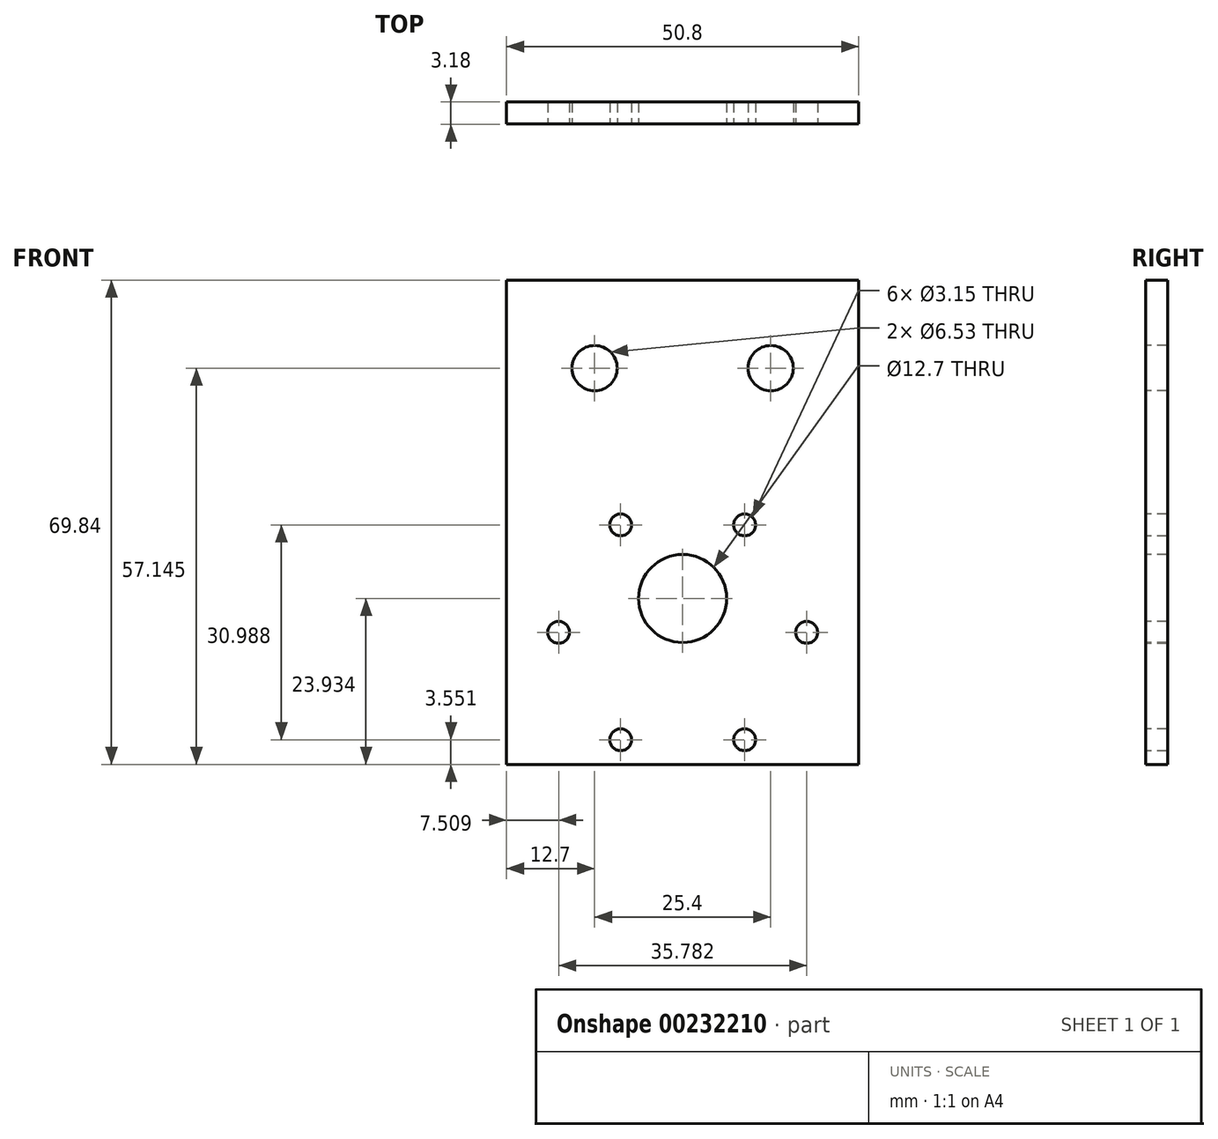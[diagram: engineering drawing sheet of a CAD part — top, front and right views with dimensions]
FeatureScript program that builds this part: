
annotation { "Feature Type Name" : "Feature", "Feature Type Description" : "" }
export const myFeature = defineFeature(function(context is Context, id is Id, definition is map)
    precondition{}
    {
        {
            var Q0;
            Q0=qCreatedBy(makeId("Front.planeOp"),FACE);
            var sketch = newSketch(context, id + "F0", { "sketchPlane" : qUnion([Q0])});
            skLineSegment(sketch, "E0.bottom", {"start": v(25.4, -34.93) * mm, "end": v(-25.4, -34.93) * mm});
            skLineSegment(sketch, "E0.top", {"start": v(25.4, 34.93) * mm, "end": v(-25.4, 34.93) * mm});
            skLineSegment(sketch, "E0.left", {"start": v(25.4, -34.93) * mm, "end": v(25.4, 34.93) * mm});
            skLineSegment(sketch, "E0.right", {"start": v(-25.4, -34.93) * mm, "end": v(-25.4, 34.93) * mm});
            skPoint(sketch, "E0.middle", {"position": v(0, 0) * mm});
            skSolve(sketch);
        }
        {
            var Q0;
            Q0=makeQuery(id+"F0.imprint","IMPRINT",FACE,{"disambiguationData":[TD([[makeQuery(id+"F0.imprint","IMPRINT",EDGE,{"derivedFrom":sQuery(id+"F0.wireOp",EDGE,"E0.bottom")}),-1.0]])]});
            extrude(context, id + "F1", {"entities" : qUnion([Q0]), "depth" : 3.17 * mm});
        }
        {
            var Q0;
            Q0=makeQuery(id+"F1.opExtrude","CAP_FACE",FACE,{"disambiguationData":[OSD([sQuery(id+"F0.wireOp",EDGE,"E0.bottom"),sQuery(id+"F0.wireOp",EDGE,"E0.top"),sQuery(id+"F0.wireOp",EDGE,"E0.left"),sQuery(id+"F0.wireOp",EDGE,"E0.right")])],"isStart":false});
            var sketch = newSketch(context, id + "F2", { "sketchPlane" : qUnion([Q0])});
            skPoint(sketch, "E1", {"position": v(-12.7, 22.23) * mm});
            skPoint(sketch, "E2", {"position": v(12.7, 22.23) * mm});
            skSolve(sketch);
        }
        {
            var Q0;
            Q0=sQuery(id+"F2.wireOp",VERTEX,"E1");
            var Q1;
            Q1=sQuery(id+"F2.wireOp",VERTEX,"E2");
            var Q2;
            Q2=makeQuery(id+"F1.opExtrude","SWEPT_BODY",BODY,{"disambiguationData":[OSD([sQuery(id+"F0.wireOp",EDGE,"E0.bottom"),sQuery(id+"F0.wireOp",EDGE,"E0.top"),sQuery(id+"F0.wireOp",EDGE,"E0.left"),sQuery(id+"F0.wireOp",EDGE,"E0.right")])]});
            hole(context, id + "F3", {"style" : HoleStyle.SIMPLE, "endStyle" : HoleEndStyle.THROUGH, "standardTappedOrClearance" : lookupTablePath({ "standard" : "ANSI", "fit" : "Close", "size" : "1/4", "type" : "Clearance" }), "standardBlindInLast" : lookupTablePath({ "fit" : "Close", "standard" : "ANSI", "size" : "1/4", "type" : "Clearance" }), "holeDiameter" : 6.53 * mm, "locations" : qUnion([Q0, Q1]), "scope" : qUnion([Q2]), "isTappedThrough" : true});
        }
        {
            var Q0;
            Q0=makeQuery(id+"F1.opExtrude","CAP_FACE",FACE,{"disambiguationData":[OSD([sQuery(id+"F0.wireOp",EDGE,"E0.bottom"),sQuery(id+"F0.wireOp",EDGE,"E0.top"),sQuery(id+"F0.wireOp",EDGE,"E0.left"),sQuery(id+"F0.wireOp",EDGE,"E0.right")])],"isStart":false});
            var sketch = newSketch(context, id + "F4", { "sketchPlane" : qUnion([Q0])});
            skCircle(sketch, "E3.cCircle", {"center": v(0, -15.88) * mm, "radius": 17.9 * mm, "construction": true});
            skLineSegment(sketch, "E3.0", {"start": v(8.95, -31.37) * mm, "end": v(-8.95, -31.37) * mm});
            skLineSegment(sketch, "E3.1", {"start": v(-8.95, -31.37) * mm, "end": v(-17.9, -15.88) * mm});
            skLineSegment(sketch, "E3.2", {"start": v(-17.9, -15.88) * mm, "end": v(-8.95, -0.38) * mm});
            skLineSegment(sketch, "E3.3", {"start": v(-8.95, -0.38) * mm, "end": v(8.95, -0.38) * mm});
            skLineSegment(sketch, "E3.4", {"start": v(8.95, -0.38) * mm, "end": v(17.9, -15.88) * mm});
            skLineSegment(sketch, "E3.5", {"start": v(17.9, -15.88) * mm, "end": v(8.95, -31.37) * mm});
            skPoint(sketch, "E4", {"position": v(-8.95, -0.38) * mm});
            skPoint(sketch, "E5", {"position": v(8.95, -0.38) * mm});
            skPoint(sketch, "E6", {"position": v(17.9, -15.88) * mm});
            skPoint(sketch, "E7", {"position": v(8.95, -31.37) * mm});
            skPoint(sketch, "E8", {"position": v(-8.95, -31.37) * mm});
            skPoint(sketch, "E9", {"position": v(-17.9, -15.88) * mm});
            skPoint(sketch, "E10", {"position": v(0, -8.86) * mm});
            skSolve(sketch);
        }
        {
            var Q0;
            Q0=sQuery(id+"F4.wireOp",VERTEX,"E4");
            var Q1;
            Q1=sQuery(id+"F4.wireOp",VERTEX,"E5");
            var Q2;
            Q2=sQuery(id+"F4.wireOp",VERTEX,"E6");
            var Q3;
            Q3=sQuery(id+"F4.wireOp",VERTEX,"E7");
            var Q4;
            Q4=sQuery(id+"F4.wireOp",VERTEX,"E8");
            var Q5;
            Q5=sQuery(id+"F4.wireOp",VERTEX,"E9");
            var Q6;
            Q6=makeQuery(id+"F1.opExtrude","SWEPT_BODY",BODY,{"disambiguationData":[OSD([sQuery(id+"F0.wireOp",EDGE,"E0.bottom"),sQuery(id+"F0.wireOp",EDGE,"E0.top"),sQuery(id+"F0.wireOp",EDGE,"E0.left"),sQuery(id+"F0.wireOp",EDGE,"E0.right")])]});
            hole(context, id + "F5", {"style" : HoleStyle.SIMPLE, "endStyle" : HoleEndStyle.THROUGH, "standardTappedOrClearance" : lookupTablePath({ "standard" : "ISO", "fit" : "Close", "size" : "M3", "type" : "Clearance" }), "standardBlindInLast" : lookupTablePath({ "fit" : "Close", "standard" : "ISO", "size" : "M3", "type" : "Clearance" }), "holeDiameter" : 3.15 * mm, "locations" : qUnion([Q0, Q1, Q2, Q3, Q4, Q5]), "scope" : qUnion([Q6]), "isTappedThrough" : true});
        }
        {
            var Q0;
            Q0=makeQuery(id+"F1.opExtrude","CAP_FACE",FACE,{"disambiguationData":[OSD([sQuery(id+"F0.wireOp",EDGE,"E0.bottom"),sQuery(id+"F0.wireOp",EDGE,"E0.top"),sQuery(id+"F0.wireOp",EDGE,"E0.left"),sQuery(id+"F0.wireOp",EDGE,"E0.right")])],"isStart":false});
            var sketch = newSketch(context, id + "F6", { "sketchPlane" : qUnion([Q0])});
            skPoint(sketch, "E11", {"position": v(0, -10.99) * mm});
            skSolve(sketch);
        }
        {
            var Q0;
            Q0=sQuery(id+"F6.wireOp",VERTEX,"E11");
            var Q1;
            Q1=makeQuery(id+"F1.opExtrude","SWEPT_BODY",BODY,{"disambiguationData":[OSD([sQuery(id+"F0.wireOp",EDGE,"E0.bottom"),sQuery(id+"F0.wireOp",EDGE,"E0.top"),sQuery(id+"F0.wireOp",EDGE,"E0.left"),sQuery(id+"F0.wireOp",EDGE,"E0.right")])]});
            hole(context, id + "F7", {"style" : HoleStyle.SIMPLE, "endStyle" : HoleEndStyle.THROUGH, "holeDiameter" : 12.7 * mm, "locations" : qUnion([Q0]), "scope" : qUnion([Q1]), "isTappedThrough" : true});
        }
    });
